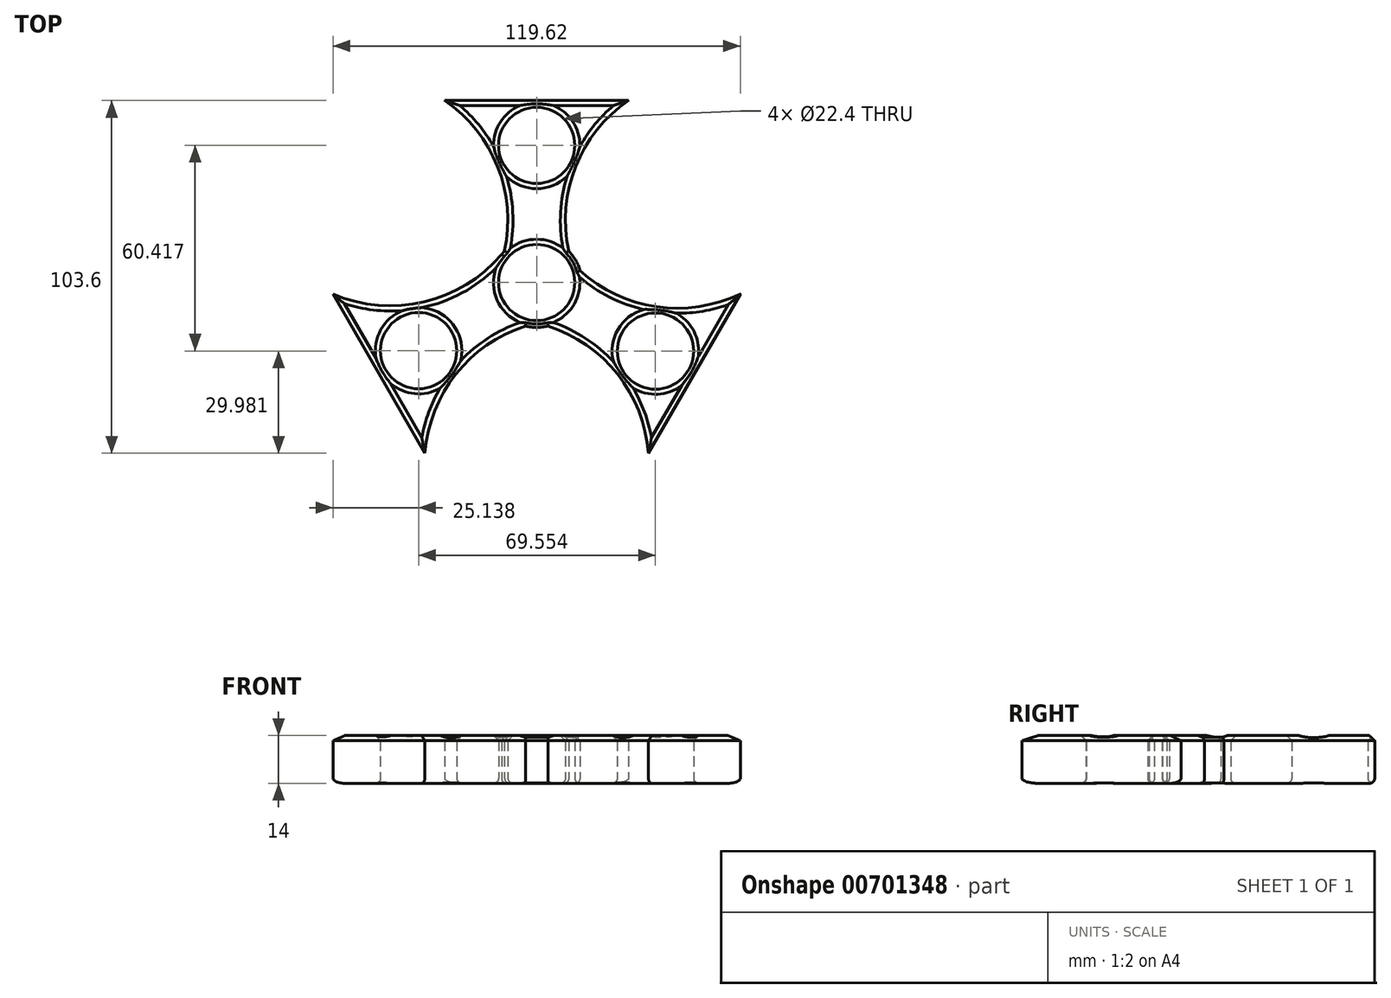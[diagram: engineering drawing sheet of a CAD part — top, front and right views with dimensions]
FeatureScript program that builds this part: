
annotation { "Feature Type Name" : "Feature", "Feature Type Description" : "" }
export const myFeature = defineFeature(function(context is Context, id is Id, definition is map)
    precondition{}
    {
        {
            var Q0;
            Q0=qCreatedBy(makeId("Top.planeOp"),FACE);
            var sketch = newSketch(context, id + "F0", { "sketchPlane" : qUnion([Q0])});
            skCircle(sketch, "E0", {"center": v(0, 0) * mm, "radius": 11.2 * mm});
            skArc(sketch, "E1", {"start": v(-3.3, -12.78) * mm, "mid": v(0, -13.2) * mm, "end": v(3.3, -12.78) * mm});
            skLineSegment(sketch, "E2", {"start": v(0, 0) * mm, "end": v(0, 29.08) * mm, "construction": true});
            skCircle(sketch, "E3", {"center": v(0, 40.28) * mm, "radius": 11.2 * mm});
            skArc(sketch, "E4", {"start": v(-12.8, 37.03) * mm, "mid": v(-12.13, 35.06) * mm, "end": v(-11.16, 33.23) * mm});
            skPoint(sketch, "E5.center", {"position": v(-0.12, 0.12) * mm});
            skArc(sketch, "E6.2.3.0", {"start": v(30.62, -6.06) * mm, "mid": v(31.02, -6.65) * mm, "end": v(31.47, -7.21) * mm});
            skLineSegment(sketch, "E7", {"start": v(0, 53.48) * mm, "end": v(-27, 53.48) * mm});
            skArc(sketch, "E8", {"start": v(-9.42, 9.24) * mm, "mid": v(-11.47, 34.04) * mm, "end": v(-27, 53.48) * mm});
            skLineSegment(sketch, "E9", {"start": v(0, 53.48) * mm, "end": v(27, 53.48) * mm});
            skArc(sketch, "E10", {"start": v(27, 53.48) * mm, "mid": v(11.47, 34.04) * mm, "end": v(9.42, 9.24) * mm});
            skLineSegment(sketch, "E11.1.0", {"start": v(-46.31, -26.74) * mm, "end": v(-59.81, -3.36) * mm});
            skLineSegment(sketch, "E11.1.1", {"start": v(-46.31, -26.74) * mm, "end": v(-32.81, -50.12) * mm});
            skArc(sketch, "E11.1.4", {"start": v(-3.3, -12.78) * mm, "mid": v(-23.74, -26.95) * mm, "end": v(-32.81, -50.12) * mm});
            skLineSegment(sketch, "E11.2.0", {"start": v(46.31, -26.74) * mm, "end": v(32.81, -50.12) * mm});
            skLineSegment(sketch, "E11.2.1", {"start": v(46.31, -26.74) * mm, "end": v(59.81, -3.36) * mm});
            skCircle(sketch, "E11.2.3", {"center": v(34.88, -20.14) * mm, "radius": 11.2 * mm});
            skArc(sketch, "E11.2.5", {"start": v(32.81, -50.12) * mm, "mid": v(23.74, -26.95) * mm, "end": v(3.3, -12.78) * mm});
            skArc(sketch, "E12.trimOffspring", {"start": v(-25.6, -29.5) * mm, "mid": v(-24.31, -28.01) * mm, "end": v(-23.26, -26.35) * mm});
            skCircle(sketch, "E13", {"center": v(-34.67, -20.02) * mm, "radius": 11.2 * mm});
            skArc(sketch, "E14.trimOffspring", {"start": v(23.24, -26.33) * mm, "mid": v(24.31, -28.02) * mm, "end": v(25.63, -29.53) * mm});
            skArc(sketch, "E15.trimOffspring", {"start": v(11.16, 33.23) * mm, "mid": v(12.13, 35.06) * mm, "end": v(12.8, 37.03) * mm});
            skArc(sketch, "E16.trimOffspring", {"start": v(12.73, 3.5) * mm, "mid": v(11.44, 6.58) * mm, "end": v(9.42, 9.24) * mm});
            skArc(sketch, "E17.trimOffspring", {"start": v(-9.42, 9.24) * mm, "mid": v(-9.87, 8.77) * mm, "end": v(-10.28, 8.28) * mm});
            skArc(sketch, "E18.trimOffspring", {"start": v(34.45, -6.95) * mm, "mid": v(36.41, -7.22) * mm, "end": v(38.38, -7.41) * mm});
            skArc(sketch, "E19", {"start": v(12.73, 3.5) * mm, "mid": v(35.23, -7.1) * mm, "end": v(59.81, -3.36) * mm});
            skArc(sketch, "E20", {"start": v(-59.81, -3.36) * mm, "mid": v(-33.13, -5.73) * mm, "end": v(-10.28, 8.28) * mm});
            skLineSegment(sketch, "E21", {"start": v(4.91, 53.48) * mm, "end": v(13.5, 53.48) * mm});
            skLineSegment(sketch, "E22", {"start": v(13.5, 53.48) * mm, "end": v(9.2, 53.48) * mm});
            skLineSegment(sketch, "E23", {"start": v(19.82, 53.48) * mm, "end": v(13.5, 53.48) * mm});
            skPoint(sketch, "E24.end.orphan", {"position": v(-19.6, 53.48) * mm});
            skSolve(sketch);
        }
        {
            var Q0;
            Q0=makeQuery(id+"F0.imprint","IMPRINT",FACE,{"disambiguationData":[TD([[makeQuery(id+"F0.imprint","IMPRINT",EDGE,{"derivedFrom":sQuery(id+"F0.wireOp",EDGE,"E0")}),-1.0]])]});
            extrude(context, id + "F1", {"entities" : qUnion([Q0]), "depth" : 7 * mm, "offsetDistance" : 25 * mm});
        }
        {
            var Q0;
            Q0=makeQuery(id+"F1.opExtrude","CAP_FACE",FACE,{"disambiguationData":[OSD([sQuery(id+"F0.wireOp",EDGE,"E0"),sQuery(id+"F0.wireOp",EDGE,"E1"),sQuery(id+"F0.wireOp",EDGE,"E3"),sQuery(id+"F0.wireOp",EDGE,"E7"),sQuery(id+"F0.wireOp",EDGE,"E8"),sQuery(id+"F0.wireOp",EDGE,"E9"),sQuery(id+"F0.wireOp",EDGE,"E10"),sQuery(id+"F0.wireOp",EDGE,"E11.1.0"),sQuery(id+"F0.wireOp",EDGE,"E11.1.1"),sQuery(id+"F0.wireOp",EDGE,"E11.1.4"),sQuery(id+"F0.wireOp",EDGE,"E11.2.0"),sQuery(id+"F0.wireOp",EDGE,"E11.2.1"),sQuery(id+"F0.wireOp",EDGE,"E11.2.3"),sQuery(id+"F0.wireOp",EDGE,"E11.2.5"),sQuery(id+"F0.wireOp",EDGE,"E13"),sQuery(id+"F0.wireOp",EDGE,"E16.trimOffspring"),sQuery(id+"F0.wireOp",EDGE,"E17.trimOffspring"),sQuery(id+"F0.wireOp",EDGE,"E19"),sQuery(id+"F0.wireOp",EDGE,"E20")])],"isStart":true});
            extrude(context, id + "F2", {"entities" : qUnion([Q0]), "operationType" : NewBodyOperationType.ADD, "depth" : 7 * mm, "offsetDistance" : 25 * mm});
        }
        {
            var Q0;
            Q0=makeQuery(id+"F2.opExtrude","CAP_FACE",FACE,{"disambiguationData":[OSD([sQuery(id+"F0.wireOp",EDGE,"E0"),sQuery(id+"F0.wireOp",EDGE,"E1"),sQuery(id+"F0.wireOp",EDGE,"E3"),sQuery(id+"F0.wireOp",EDGE,"E7"),sQuery(id+"F0.wireOp",EDGE,"E8"),sQuery(id+"F0.wireOp",EDGE,"E9"),sQuery(id+"F0.wireOp",EDGE,"E10"),sQuery(id+"F0.wireOp",EDGE,"E11.1.0"),sQuery(id+"F0.wireOp",EDGE,"E11.1.1"),sQuery(id+"F0.wireOp",EDGE,"E11.1.4"),sQuery(id+"F0.wireOp",EDGE,"E11.2.0"),sQuery(id+"F0.wireOp",EDGE,"E11.2.1"),sQuery(id+"F0.wireOp",EDGE,"E11.2.3"),sQuery(id+"F0.wireOp",EDGE,"E11.2.5"),sQuery(id+"F0.wireOp",EDGE,"E13"),sQuery(id+"F0.wireOp",EDGE,"E16.trimOffspring"),sQuery(id+"F0.wireOp",EDGE,"E17.trimOffspring"),sQuery(id+"F0.wireOp",EDGE,"E19"),sQuery(id+"F0.wireOp",EDGE,"E20")])],"isStart":false});
            fillet(context, id + "F3", {"entities" : qUnion([Q0]), "radius" : 1.5 * mm, "tangentPropagation" : true, "allowEdgeOverflow" : false});
        }
        {
            var Q0;
            Q0=makeQuery(id+"F1.opExtrude","CAP_FACE",FACE,{"disambiguationData":[OSD([sQuery(id+"F0.wireOp",EDGE,"E0"),sQuery(id+"F0.wireOp",EDGE,"E1"),sQuery(id+"F0.wireOp",EDGE,"E3"),sQuery(id+"F0.wireOp",EDGE,"E7"),sQuery(id+"F0.wireOp",EDGE,"E8"),sQuery(id+"F0.wireOp",EDGE,"E9"),sQuery(id+"F0.wireOp",EDGE,"E10"),sQuery(id+"F0.wireOp",EDGE,"E11.1.0"),sQuery(id+"F0.wireOp",EDGE,"E11.1.1"),sQuery(id+"F0.wireOp",EDGE,"E11.1.4"),sQuery(id+"F0.wireOp",EDGE,"E11.2.0"),sQuery(id+"F0.wireOp",EDGE,"E11.2.1"),sQuery(id+"F0.wireOp",EDGE,"E11.2.3"),sQuery(id+"F0.wireOp",EDGE,"E11.2.5"),sQuery(id+"F0.wireOp",EDGE,"E13"),sQuery(id+"F0.wireOp",EDGE,"E16.trimOffspring"),sQuery(id+"F0.wireOp",EDGE,"E17.trimOffspring"),sQuery(id+"F0.wireOp",EDGE,"E19"),sQuery(id+"F0.wireOp",EDGE,"E20")])],"isStart":false});
            chamfer(context, id + "F4", {"entities" : qUnion([Q0]), "width" : 1.5 * mm, "tangentPropagation" : true});
        }
    });
